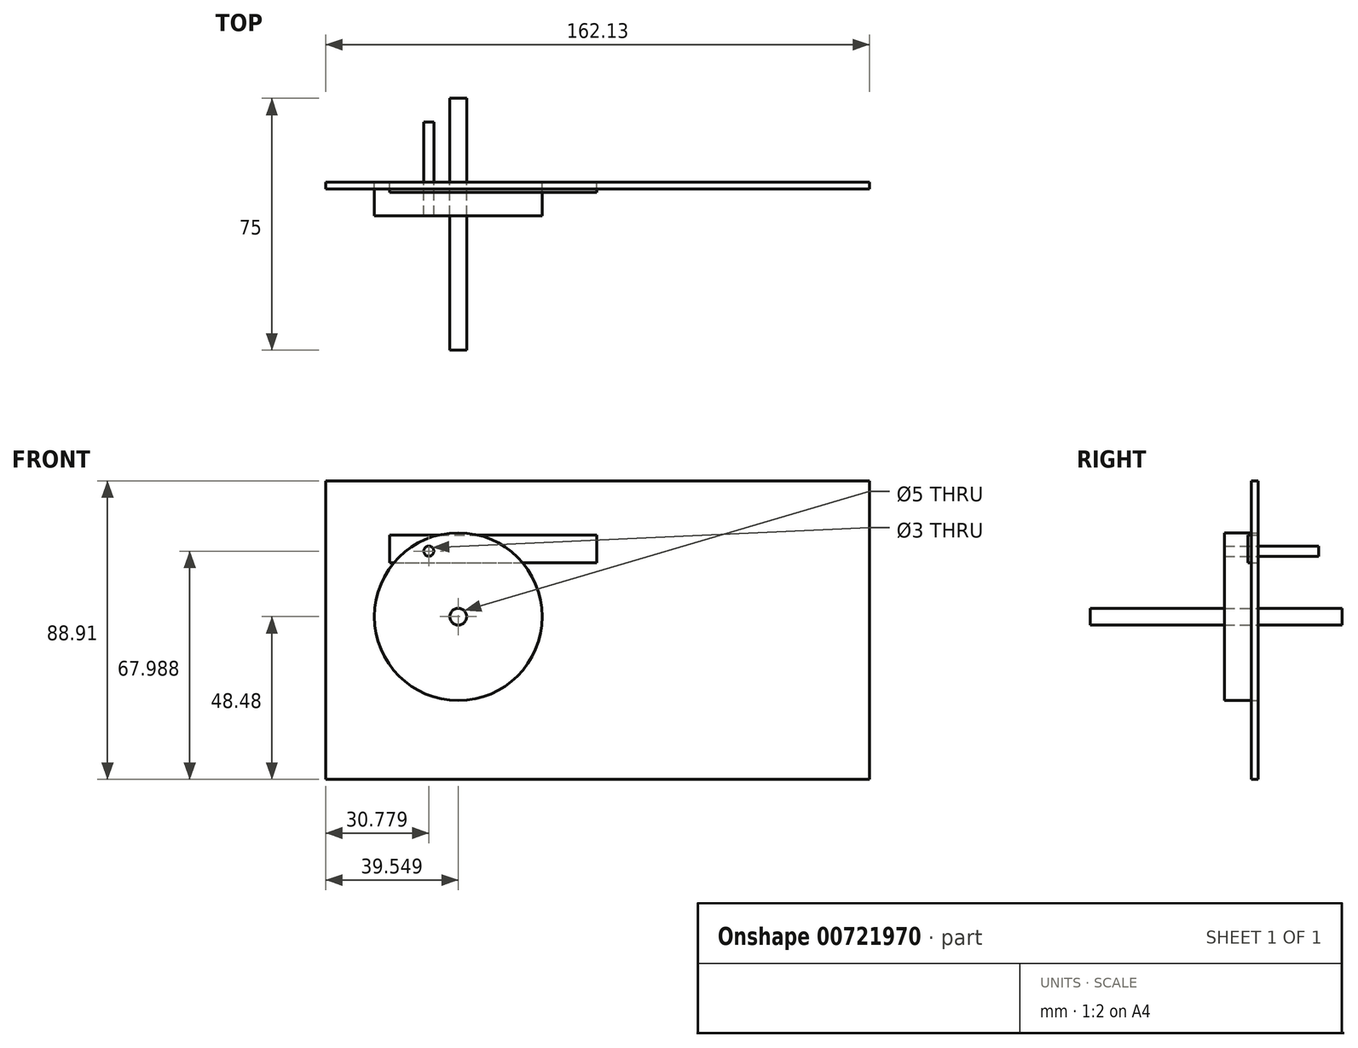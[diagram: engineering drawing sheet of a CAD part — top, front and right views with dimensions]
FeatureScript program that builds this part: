
annotation { "Feature Type Name" : "Feature", "Feature Type Description" : "" }
export const myFeature = defineFeature(function(context is Context, id is Id, definition is map)
    precondition{}
    {
        {
            var Q0;
            Q0=qCreatedBy(makeId("Front.planeOp"),FACE);
            var sketch = newSketch(context, id + "F0", { "sketchPlane" : qUnion([Q0])});
            skCircle(sketch, "E0", {"center": v(-51.74, 0) * mm, "radius": 25 * mm});
            skCircle(sketch, "E1", {"center": v(-51.74, 0) * mm, "radius": 2.5 * mm});
            skCircle(sketch, "E2", {"center": v(-60.51, 19.5) * mm, "radius": 1.5 * mm});
            skSolve(sketch);
        }
        {
            var Q0;
            Q0 = qSketchRegion(id + "F0", true);
            extrude(context, id + "F1", {"entities" : qUnion([Q0]), "depth" : 10 * mm, "offsetDistance" : 25 * mm});
        }
        {
            var Q0;
            Q0=makeQuery(id+"F0.imprint","IMPRINT",FACE,{"disambiguationData":[TD([[makeQuery(id+"F0.imprint","IMPRINT",EDGE,{"derivedFrom":sQuery(id+"F0.wireOp",EDGE,"E1")}),1.0]])]});
            var Q1;
            Q1=sQuery(id+"F0.wireOp",EDGE,"E1");
            extrude(context, id + "F2", {"entities" : qUnion([Q0]), "surfaceEntities" : qUnion([Q1]), "depth" : 50 * mm, "offsetDistance" : 25 * mm, "hasSecondDirection" : true, "secondDirectionOppositeDirection" : true, "secondDirectionDepth" : 25 * mm});
        }
        {
            var Q0;
            Q0=qCreatedBy(makeId("Front.planeOp"),FACE);
            var sketch = newSketch(context, id + "F3", { "sketchPlane" : qUnion([Q0])});
            skLineSegment(sketch, "E3.bottom", {"start": v(-91.29, 40.43) * mm, "end": v(70.84, 40.43) * mm});
            skLineSegment(sketch, "E3.top", {"start": v(-91.29, -48.48) * mm, "end": v(70.84, -48.48) * mm});
            skLineSegment(sketch, "E3.left", {"start": v(-91.29, 40.43) * mm, "end": v(-91.29, -48.48) * mm});
            skLineSegment(sketch, "E3.right", {"start": v(70.84, 40.43) * mm, "end": v(70.84, -48.48) * mm});
            skSolve(sketch);
        }
        {
            var Q0;
            Q0=makeQuery(id+"F3.imprint","IMPRINT",FACE,{"disambiguationData":[TD([[makeQuery(id+"F3.imprint","IMPRINT",EDGE,{"derivedFrom":sQuery(id+"F3.wireOp",EDGE,"E3.bottom")}),-1.0]])]});
            extrude(context, id + "F4", {"entities" : qUnion([Q0]), "depth" : 2 * mm, "offsetDistance" : 25 * mm});
        }
        {
            var Q0;
            Q0=makeQuery(id+"F0.imprint","IMPRINT",FACE,{"disambiguationData":[TD([[makeQuery(id+"F0.imprint","IMPRINT",EDGE,{"derivedFrom":sQuery(id+"F0.wireOp",EDGE,"E2")}),1.0]])]});
            extrude(context, id + "F5", {"entities" : qUnion([Q0]), "oppositeDirection" : true, "depth" : 18 * mm, "offsetDistance" : 25 * mm});
        }
        {
            var Q0;
            Q0=qCreatedBy(makeId("Front.planeOp"),FACE);
            var sketch = newSketch(context, id + "F6", { "sketchPlane" : qUnion([Q0])});
            skLineSegment(sketch, "E4.bottom", {"start": v(-72.18, 24.34) * mm, "end": v(-10.42, 24.34) * mm});
            skLineSegment(sketch, "E4.top", {"start": v(-72.18, 16.09) * mm, "end": v(-10.42, 16.09) * mm});
            skLineSegment(sketch, "E4.left", {"start": v(-72.18, 24.34) * mm, "end": v(-72.18, 16.09) * mm});
            skLineSegment(sketch, "E4.right", {"start": v(-10.42, 24.34) * mm, "end": v(-10.42, 16.09) * mm});
            skSolve(sketch);
        }
        {
            var Q0;
            Q0=makeQuery(id+"F0.imprint","IMPRINT",FACE,{"disambiguationData":[TD([[makeQuery(id+"F0.imprint","IMPRINT",EDGE,{"derivedFrom":sQuery(id+"F0.wireOp",EDGE,"E2")}),1.0]])]});
            var Q1;
            Q1=makeQuery(id+"F6.imprint","IMPRINT",FACE,{"disambiguationData":[TD([[makeQuery(id+"F6.imprint","IMPRINT",EDGE,{"derivedFrom":sQuery(id+"F6.wireOp",EDGE,"E4.bottom")}),-1.0]])]});
            extrude(context, id + "F7", {"entities" : qUnion([Q0, Q1]), "depth" : 3 * mm, "offsetDistance" : 25 * mm});
        }
        {
            var Q0;
            Q0=makeQuery(id+"F7.opExtrude","SWEPT_BODY",BODY,{"disambiguationData":[OSD([sQuery(id+"F0.wireOp",EDGE,"E2")])]});
            deleteBodies(context, id + "F8", {"entities" : qUnion([Q0])});
        }
    });
